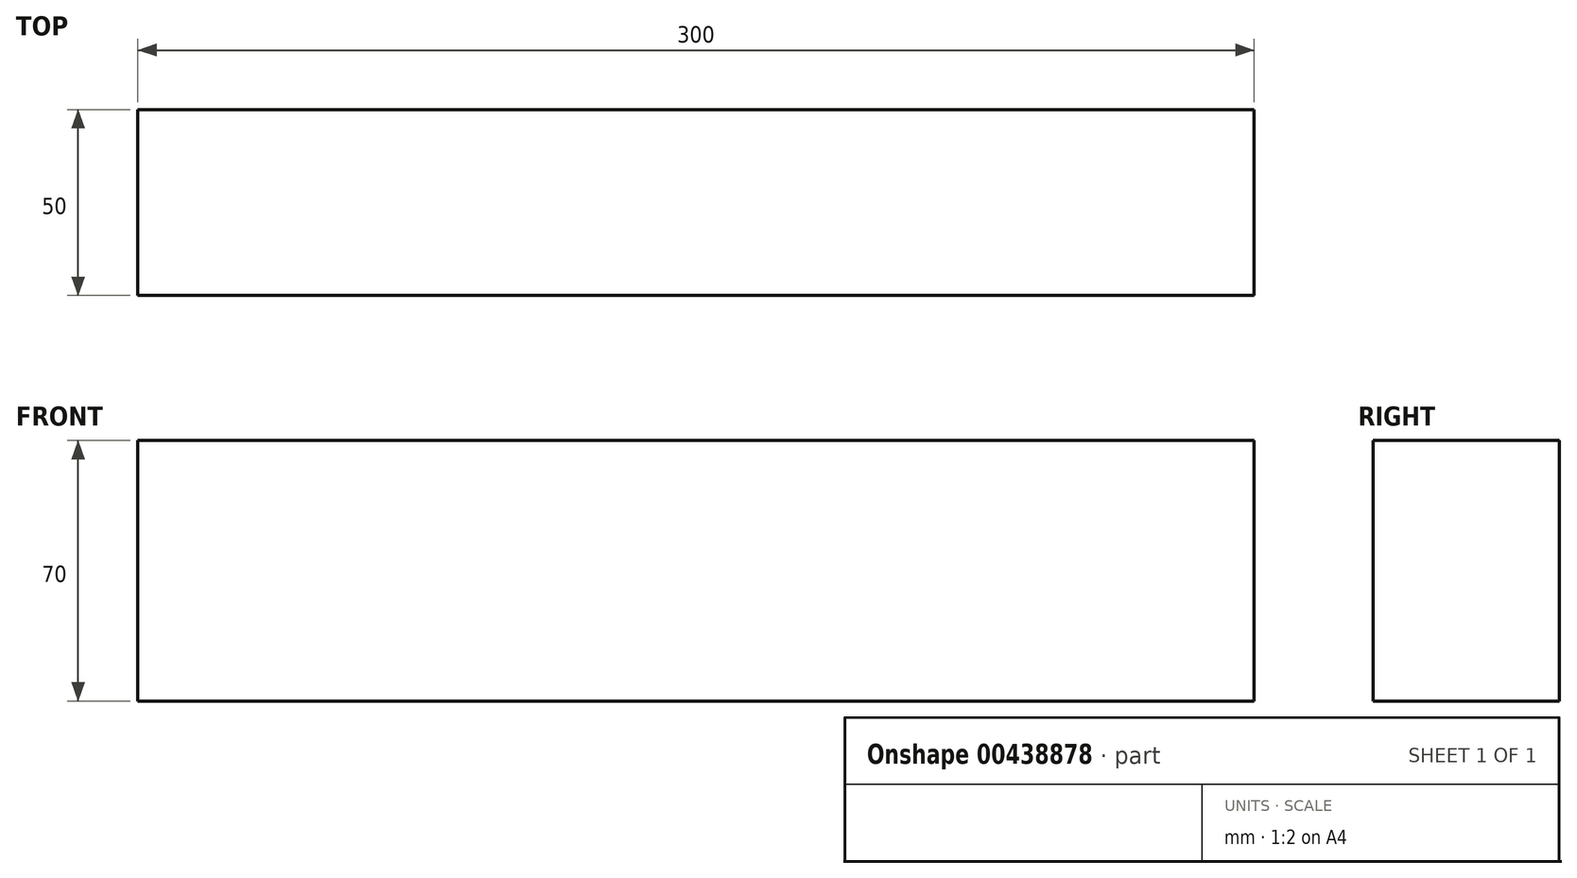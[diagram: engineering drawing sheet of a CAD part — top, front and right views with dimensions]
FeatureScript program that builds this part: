
annotation { "Feature Type Name" : "Feature", "Feature Type Description" : "" }
export const myFeature = defineFeature(function(context is Context, id is Id, definition is map)
    precondition{}
    {
        {
            var Q0;
            Q0=qCreatedBy(makeId("Right.planeOp"),FACE);
            var sketch = newSketch(context, id + "F0", { "sketchPlane" : qUnion([Q0])});
            skLineSegment(sketch, "E0.bottom", {"start": v(25, -35) * mm, "end": v(-25, -35) * mm});
            skLineSegment(sketch, "E0.top", {"start": v(25, 35) * mm, "end": v(-25, 35) * mm});
            skLineSegment(sketch, "E0.left", {"start": v(25, -35) * mm, "end": v(25, 35) * mm});
            skLineSegment(sketch, "E0.right", {"start": v(-25, -35) * mm, "end": v(-25, 35) * mm});
            skPoint(sketch, "E0.middle", {"position": v(0, 0) * mm});
            skSolve(sketch);
        }
        {
            var Q0;
            Q0=makeQuery(id+"F0.imprint","IMPRINT",FACE,{"disambiguationData":[TD([[makeQuery(id+"F0.imprint","IMPRINT",EDGE,{"derivedFrom":sQuery(id+"F0.wireOp",EDGE,"E0.bottom")}),-1.0]])]});
            extrude(context, id + "F1", {"entities" : qUnion([Q0]), "depth" : 300 * mm});
        }
    });
